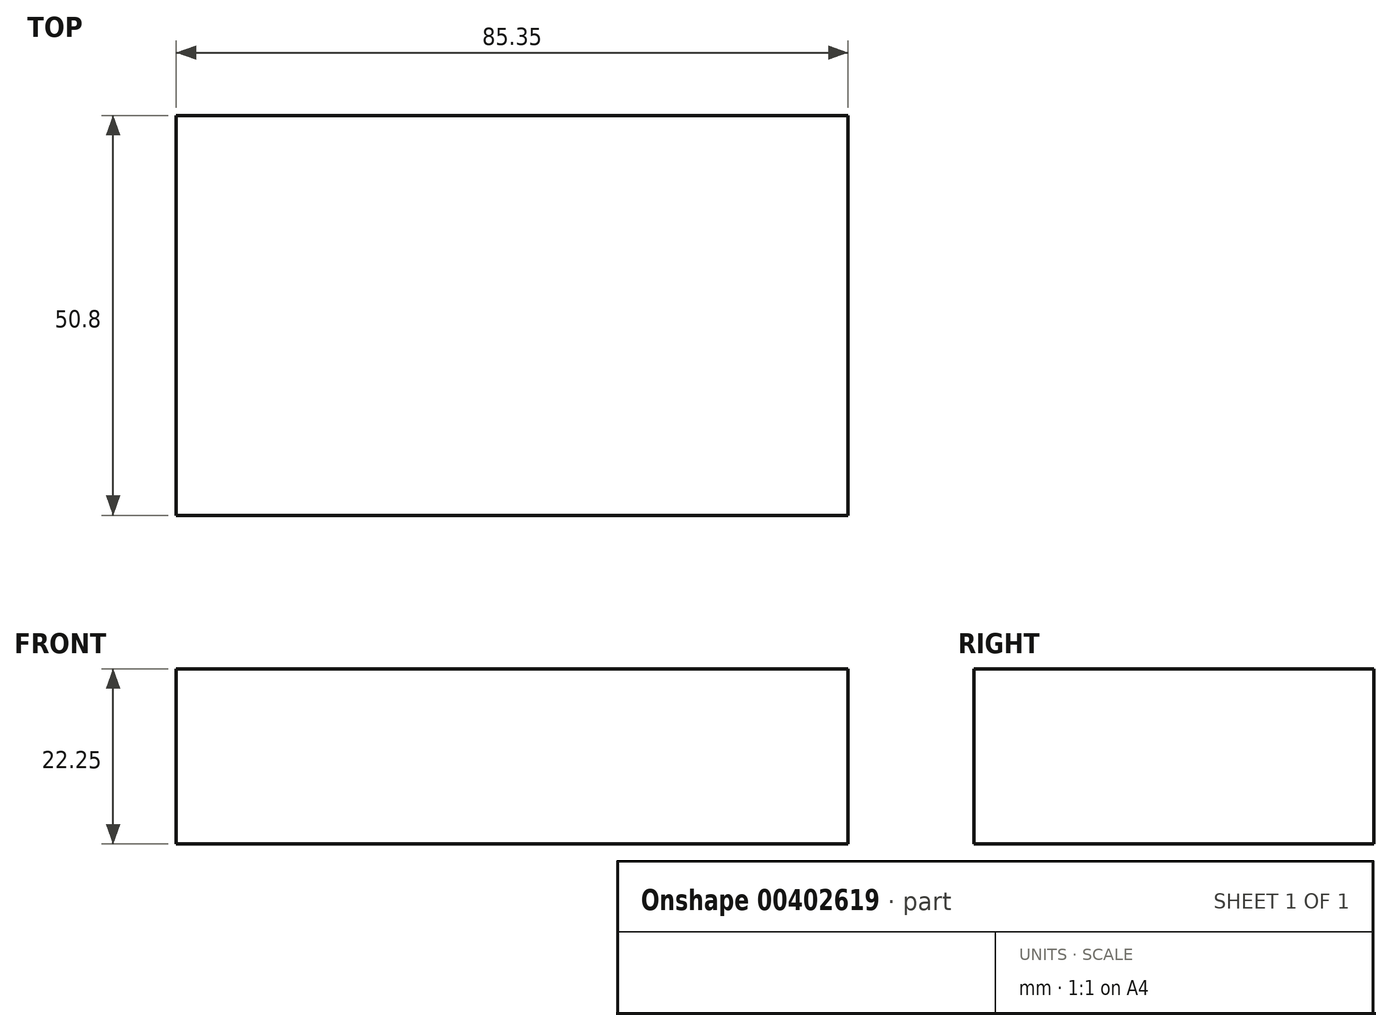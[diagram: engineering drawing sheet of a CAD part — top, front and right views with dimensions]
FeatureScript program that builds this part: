
annotation { "Feature Type Name" : "Feature", "Feature Type Description" : "" }
export const myFeature = defineFeature(function(context is Context, id is Id, definition is map)
    precondition{}
    {
        {
            var Q0;
            Q0=qCreatedBy(makeId("Front.planeOp"),FACE);
            var sketch = newSketch(context, id + "F0", { "sketchPlane" : qUnion([Q0])});
            skLineSegment(sketch, "E0.bottom", {"start": v(-43.59, 52.27) * mm, "end": v(41.76, 52.27) * mm});
            skLineSegment(sketch, "E0.top", {"start": v(-43.59, 30.02) * mm, "end": v(41.76, 30.02) * mm});
            skLineSegment(sketch, "E0.left", {"start": v(-43.59, 52.27) * mm, "end": v(-43.59, 30.02) * mm});
            skLineSegment(sketch, "E0.right", {"start": v(41.76, 52.27) * mm, "end": v(41.76, 30.02) * mm});
            skSolve(sketch);
        }
        {
            var Q0;
            Q0 = qSketchRegion(id + "F0", true);
            extrude(context, id + "F1", {"entities" : qUnion([Q0]), "depth" : 50.8 * mm});
        }
    });
